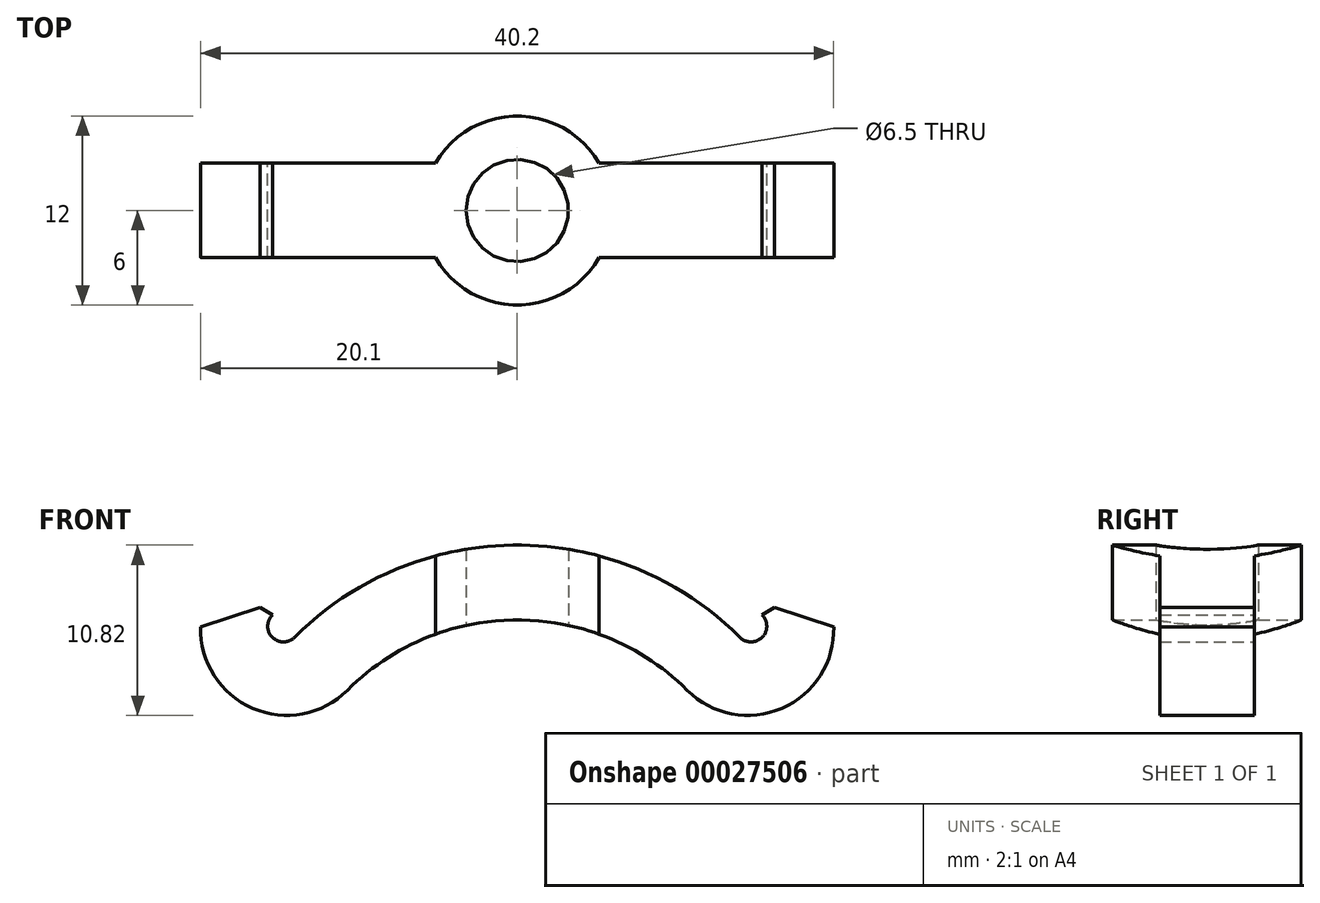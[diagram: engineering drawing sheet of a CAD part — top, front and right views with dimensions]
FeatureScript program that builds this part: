
annotation { "Feature Type Name" : "Feature", "Feature Type Description" : "" }
export const myFeature = defineFeature(function(context is Context, id is Id, definition is map)
    precondition{}
    {
        {
            var Q0;
            Q0=qCreatedBy(makeId("Front.planeOp"),FACE);
            var sketch = newSketch(context, id + "F0", { "sketchPlane" : qUnion([Q0])});
            skArc(sketch, "E0", {"start": v(10.78, 10.78) * mm, "mid": v(0, 15.25) * mm, "end": v(-10.78, 10.78) * mm});
            skArc(sketch, "E1", {"start": v(17.37, 9.91) * mm, "mid": v(2.66, 19.82) * mm, "end": v(-14.14, 14.14) * mm});
            skLineSegment(sketch, "E2", {"start": v(0, 0) * mm, "end": v(-10.78, 10.78) * mm, "construction": true});
            skLineSegment(sketch, "E3", {"start": v(0, 0) * mm, "end": v(10.78, 10.78) * mm, "construction": true});
            skArc(sketch, "E4", {"start": v(-10.78, 10.78) * mm, "mid": v(-16.81, 9.63) * mm, "end": v(-20.1, 14.82) * mm});
            skArc(sketch, "E5", {"start": v(-14.14, 14.14) * mm, "mid": v(-15.57, 14.15) * mm, "end": v(-15.53, 15.58) * mm});
            skLineSegment(sketch, "E6.trimOffspring", {"start": v(-14.64, 14.64) * mm, "end": v(-14.85, 14.85) * mm});
            skLineSegment(sketch, "E7", {"start": v(-15.53, 15.58) * mm, "end": v(-16.33, 16.05) * mm});
            skLineSegment(sketch, "E8", {"start": v(-16.33, 16.05) * mm, "end": v(-20.1, 14.82) * mm});
            skLineSegment(sketch, "E9", {"start": v(0, 0) * mm, "end": v(0, 31.06) * mm, "construction": true});
            skArc(sketch, "E10.MirrorCS", {"start": v(14.14, 14.14) * mm, "mid": v(15.57, 14.15) * mm, "end": v(15.53, 15.58) * mm});
            skLineSegment(sketch, "E11.MirrorCS", {"start": v(15.53, 15.58) * mm, "end": v(16.33, 16.05) * mm});
            skLineSegment(sketch, "E12.MirrorCS", {"start": v(16.33, 16.05) * mm, "end": v(20.1, 14.82) * mm});
            skArc(sketch, "E13.MirrorCS", {"start": v(10.78, 10.78) * mm, "mid": v(16.81, 9.63) * mm, "end": v(20.1, 14.82) * mm});
            skPoint(sketch, "E14.MirrorCS.end.orphan", {"position": v(-10.78, 10.78) * mm});
            skPoint(sketch, "E15.MirrorCS.end.orphan", {"position": v(10.78, 10.78) * mm});
            skSolve(sketch);
        }
        {
            var Q0;
            Q0 = qSketchRegion(id + "F0", true);
            extrude(context, id + "F1", {"entities" : qUnion([Q0]), "endBound" : BoundingType.SYMMETRIC, "depth" : 12 * mm});
        }
        {
            var Q0;
            Q0=qCreatedBy(makeId("Top.planeOp"),FACE);
            var sketch = newSketch(context, id + "F2", { "sketchPlane" : qUnion([Q0])});
            skArc(sketch, "E16", {"start": v(-5.2, -3) * mm, "mid": v(0, -6) * mm, "end": v(5.2, -3) * mm});
            skCircle(sketch, "E17", {"center": v(0, 0) * mm, "radius": 3.25 * mm});
            skLineSegment(sketch, "E18", {"start": v(-5.2, 3) * mm, "end": v(-20.73, 3) * mm});
            skLineSegment(sketch, "E19", {"start": v(-20.73, 3) * mm, "end": v(-20.73, 6.92) * mm});
            skLineSegment(sketch, "E20", {"start": v(-20.73, 6.92) * mm, "end": v(21.59, 6.92) * mm});
            skLineSegment(sketch, "E21", {"start": v(21.59, 6.92) * mm, "end": v(21.59, 3) * mm});
            skLineSegment(sketch, "E22", {"start": v(21.59, 3) * mm, "end": v(5.2, 3) * mm});
            skLineSegment(sketch, "E23", {"start": v(0, 0) * mm, "end": v(-22.81, 0) * mm, "construction": true});
            skLineSegment(sketch, "E24.MirrorCS", {"start": v(-5.2, -3) * mm, "end": v(-20.73, -3) * mm});
            skLineSegment(sketch, "E25.MirrorCS", {"start": v(-20.73, -3) * mm, "end": v(-20.73, -6.92) * mm});
            skLineSegment(sketch, "E26.MirrorCS", {"start": v(-20.73, -6.92) * mm, "end": v(21.59, -6.92) * mm});
            skLineSegment(sketch, "E27.MirrorCS", {"start": v(21.59, -6.92) * mm, "end": v(21.59, -3) * mm});
            skLineSegment(sketch, "E28.MirrorCS", {"start": v(21.59, -3) * mm, "end": v(5.2, -3) * mm});
            skArc(sketch, "E29.trimOffspring", {"start": v(5.2, 3) * mm, "mid": v(0, 6) * mm, "end": v(-5.2, 3) * mm});
            skSolve(sketch);
        }
        {
            var Q0;
            Q0 = qSketchRegion(id + "F2", true);
            extrude(context, id + "F3", {"entities" : qUnion([Q0]), "operationType" : NewBodyOperationType.REMOVE, "depth" : 25 * mm});
        }
    });
